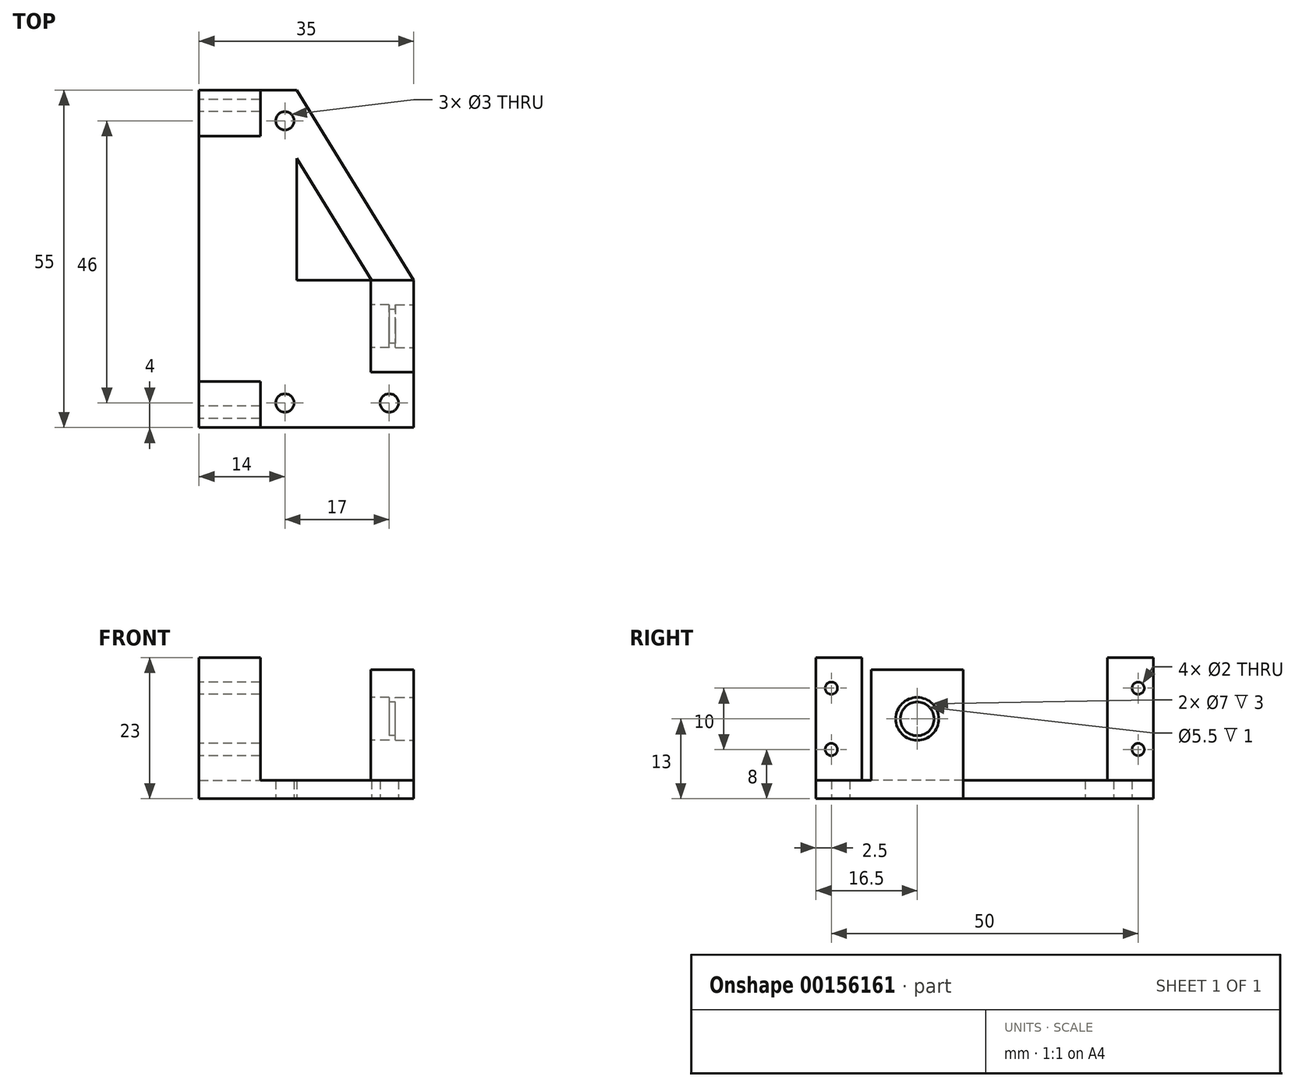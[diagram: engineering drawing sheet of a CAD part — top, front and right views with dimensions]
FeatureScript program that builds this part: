
annotation { "Feature Type Name" : "Feature", "Feature Type Description" : "" }
export const myFeature = defineFeature(function(context is Context, id is Id, definition is map)
    precondition{}
    {
        {
            var Q0;
            Q0=qCreatedBy(makeId("Top.planeOp"),FACE);
            var sketch = newSketch(context, id + "F0", { "sketchPlane" : qUnion([Q0])});
            skLineSegment(sketch, "E0.bottom", {"start": v(0, 0) * mm, "end": v(35, 0) * mm});
            skLineSegment(sketch, "E0.top", {"start": v(0, 55) * mm, "end": v(15.93, 55) * mm});
            skLineSegment(sketch, "E0.left", {"start": v(0, 0) * mm, "end": v(0, 55) * mm});
            skLineSegment(sketch, "E0.right", {"start": v(35, 0) * mm, "end": v(35, 24) * mm});
            skLineSegment(sketch, "E1", {"start": v(15.93, 43.86) * mm, "end": v(15.93, 24) * mm});
            skLineSegment(sketch, "E2", {"start": v(15.93, 24) * mm, "end": v(28.15, 24) * mm});
            skLineSegment(sketch, "E3", {"start": v(15.93, 55) * mm, "end": v(35, 24) * mm});
            skLineSegment(sketch, "E4", {"start": v(28.15, 24) * mm, "end": v(15.93, 43.86) * mm});
            skCircle(sketch, "E5", {"center": v(14, 50) * mm, "radius": 1.5 * mm});
            skCircle(sketch, "E6", {"center": v(14, 4) * mm, "radius": 1.5 * mm});
            skCircle(sketch, "E7", {"center": v(31, 4) * mm, "radius": 1.5 * mm});
            skSolve(sketch);
        }
        {
            var Q0;
            Q0 = qSketchRegion(id + "F0", true);
            extrude(context, id + "F1", {"entities" : qUnion([Q0]), "depth" : 3 * mm});
        }
        {
            var Q0;
            Q0=makeQuery(id+"F1.opExtrude","CAP_FACE",FACE,{"disambiguationData":[OSD([sQuery(id+"F0.wireOp",EDGE,"E0.bottom"),sQuery(id+"F0.wireOp",EDGE,"E0.top"),sQuery(id+"F0.wireOp",EDGE,"E0.left"),sQuery(id+"F0.wireOp",EDGE,"E0.right")])],"isStart":false});
            var sketch = newSketch(context, id + "F2", { "sketchPlane" : qUnion([Q0])});
            skLineSegment(sketch, "E8.bottom", {"start": v(0, 0) * mm, "end": v(10, 0) * mm});
            skLineSegment(sketch, "E8.top", {"start": v(0, 7.5) * mm, "end": v(10, 7.5) * mm});
            skLineSegment(sketch, "E8.left", {"start": v(0, 0) * mm, "end": v(0, 7.5) * mm});
            skLineSegment(sketch, "E8.right", {"start": v(10, 0) * mm, "end": v(10, 7.5) * mm});
            skLineSegment(sketch, "E9.bottom", {"start": v(0, 47.5) * mm, "end": v(10, 47.5) * mm});
            skLineSegment(sketch, "E9.top", {"start": v(0, 55) * mm, "end": v(10, 55) * mm});
            skLineSegment(sketch, "E9.left", {"start": v(0, 47.5) * mm, "end": v(0, 55) * mm});
            skLineSegment(sketch, "E9.right", {"start": v(10, 47.5) * mm, "end": v(10, 55) * mm});
            skLineSegment(sketch, "E10.bottom", {"start": v(28, 24) * mm, "end": v(35, 24) * mm});
            skLineSegment(sketch, "E10.top", {"start": v(28, 9) * mm, "end": v(35, 9) * mm});
            skLineSegment(sketch, "E10.left", {"start": v(28, 24) * mm, "end": v(28, 9) * mm});
            skLineSegment(sketch, "E10.right", {"start": v(35, 24) * mm, "end": v(35, 9) * mm});
            skLineSegment(sketch, "E11", {"start": v(0, 14.55) * mm, "end": v(34, 14.55) * mm, "construction": true});
            skSolve(sketch);
        }
        {
            var Q0;
            Q0=makeQuery(id+"F2.imprint","IMPRINT",FACE,{"disambiguationData":[TD([[makeQuery(id+"F2.imprint","IMPRINT",EDGE,{"derivedFrom":sQuery(id+"F2.wireOp",EDGE,"E10.bottom")}),-1.0]])]});
            extrude(context, id + "F3", {"entities" : qUnion([Q0]), "operationType" : NewBodyOperationType.ADD, "depth" : 18 * mm});
        }
        {
            var Q0;
            Q0=makeQuery(id+"F2.imprint","IMPRINT",FACE,{"disambiguationData":[TD([[makeQuery(id+"F2.imprint","IMPRINT",EDGE,{"derivedFrom":sQuery(id+"F2.wireOp",EDGE,"E8.bottom")}),1.0]])]});
            var Q1;
            Q1=makeQuery(id+"F2.imprint","IMPRINT",FACE,{"disambiguationData":[TD([[makeQuery(id+"F2.imprint","IMPRINT",EDGE,{"derivedFrom":sQuery(id+"F2.wireOp",EDGE,"E9.bottom")}),1.0]])]});
            extrude(context, id + "F4", {"entities" : qUnion([Q0, Q1]), "operationType" : NewBodyOperationType.ADD, "depth" : 20 * mm});
        }
        {
            var Q0;
            Q0=makeQuery(id+"F3.opExtrude","SWEPT_FACE",FACE,{"disambiguationData":[OSD([sQuery(id+"F2.wireOp",EDGE,"E10.left")])]});
            var sketch = newSketch(context, id + "F5", { "sketchPlane" : qUnion([Q0])});
            skCircle(sketch, "E12", {"center": v(-16.5, 13) * mm, "radius": 3.5 * mm});
            skPoint(sketch, "E12.centerSnap0", {"position": v(-16.5, 21) * mm});
            skSolve(sketch);
        }
        {
            var Q0;
            Q0 = qSketchRegion(id + "F5", true);
            extrude(context, id + "F6", {"entities" : qUnion([Q0]), "operationType" : NewBodyOperationType.REMOVE, "oppositeDirection" : true, "depth" : 3 * mm});
        }
        {
            var Q0;
            Q0=makeQuery(id+"F6.boolean.opBoolean","COPY",FACE,{"derivedFrom":makeQuery(id+"F6.opExtrude","CAP_FACE",FACE,{"disambiguationData":[OSD([sQuery(id+"F5.wireOp",EDGE,"E12")])],"isStart":false})});
            var sketch = newSketch(context, id + "F7", { "sketchPlane" : qUnion([Q0])});
            skCircle(sketch, "E13", {"center": v(-16.5, 13) * mm, "radius": 2.75 * mm});
            skSolve(sketch);
        }
        {
            var Q0;
            Q0 = qSketchRegion(id + "F7", true);
            extrude(context, id + "F8", {"entities" : qUnion([Q0]), "operationType" : NewBodyOperationType.REMOVE, "oppositeDirection" : true, "depth" : 25 * mm});
        }
        {
            var Q0;
            Q0=makeQuery(id+"F4.boolean.opBoolean","MERGE",FACE,{"derivedFrom":[makeQuery(id+"F1.opExtrude","SWEPT_FACE",FACE,{"disambiguationData":[OSD([sQuery(id+"F0.wireOp",EDGE,"E0.left")])]}),makeQuery(id+"F4.opExtrude","SWEPT_FACE",FACE,{"disambiguationData":[OSD([sQuery(id+"F2.wireOp",EDGE,"E8.left")])]}),makeQuery(id+"F4.opExtrude","SWEPT_FACE",FACE,{"disambiguationData":[OSD([sQuery(id+"F2.wireOp",EDGE,"E9.left")])]})]});
            var sketch = newSketch(context, id + "F9", { "sketchPlane" : qUnion([Q0])});
            skCircle(sketch, "E14", {"center": v(-2.5, 18) * mm, "radius": 1 * mm});
            skCircle(sketch, "E15", {"center": v(-2.5, 8) * mm, "radius": 1 * mm});
            skCircle(sketch, "E16", {"center": v(-52.5, 18) * mm, "radius": 1 * mm});
            skCircle(sketch, "E17", {"center": v(-52.5, 8) * mm, "radius": 1 * mm});
            skSolve(sketch);
        }
        {
            var Q0;
            Q0 = qSketchRegion(id + "F9", true);
            extrude(context, id + "F10", {"entities" : qUnion([Q0]), "operationType" : NewBodyOperationType.REMOVE, "oppositeDirection" : true, "depth" : 25 * mm});
        }
        {
            var Q0;
            Q0=makeQuery(id+"F3.boolean.opBoolean","MERGE",FACE,{"derivedFrom":[makeQuery(id+"F1.opExtrude","SWEPT_FACE",FACE,{"disambiguationData":[OSD([sQuery(id+"F0.wireOp",EDGE,"E0.right")])]}),makeQuery(id+"F3.opExtrude","SWEPT_FACE",FACE,{"disambiguationData":[OSD([sQuery(id+"F2.wireOp",EDGE,"E10.right")])]})]});
            var sketch = newSketch(context, id + "F11", { "sketchPlane" : qUnion([Q0])});
            skCircle(sketch, "E18", {"center": v(16.5, 13) * mm, "radius": 3.5 * mm});
            skSolve(sketch);
        }
        {
            var Q0;
            Q0 = qSketchRegion(id + "F11", true);
            extrude(context, id + "F12", {"entities" : qUnion([Q0]), "operationType" : NewBodyOperationType.REMOVE, "oppositeDirection" : true, "depth" : 3 * mm});
        }
    });
